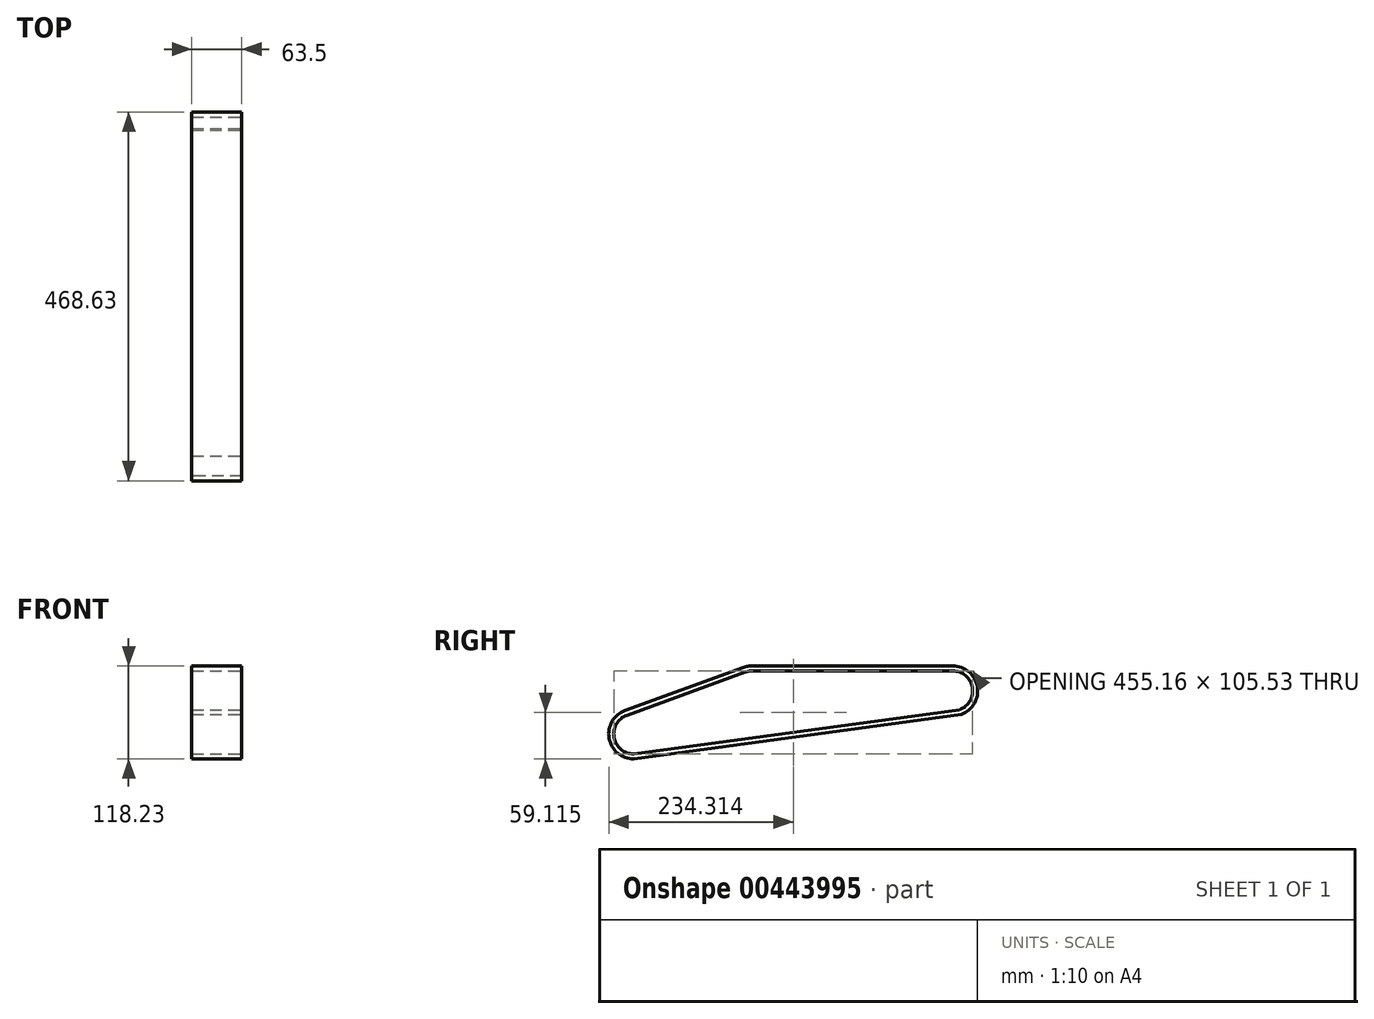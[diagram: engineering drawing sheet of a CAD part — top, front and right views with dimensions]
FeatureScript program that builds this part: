
annotation { "Feature Type Name" : "Feature", "Feature Type Description" : "" }
export const myFeature = defineFeature(function(context is Context, id is Id, definition is map)
    precondition{}
    {
        {
            var Q0;
            Q0=qCreatedBy(makeId("Front.planeOp"),FACE);
            var sketch = newSketch(context, id + "F0", { "sketchPlane" : qUnion([Q0])});
            skLineSegment(sketch, "E0.bottom", {"start": v(0, 0) * mm, "end": v(63.5, 0) * mm});
            skLineSegment(sketch, "E0.top", {"start": v(0, 6.35) * mm, "end": v(63.5, 6.35) * mm});
            skLineSegment(sketch, "E0.left", {"start": v(0, 0) * mm, "end": v(0, 6.35) * mm});
            skLineSegment(sketch, "E0.right", {"start": v(63.5, 0) * mm, "end": v(63.5, 6.35) * mm});
            skSolve(sketch);
        }
        {
            var Q0;
            Q0=makeQuery(id+"F0.imprint","IMPRINT",FACE,{"disambiguationData":[TD([[makeQuery(id+"F0.imprint","IMPRINT",EDGE,{"derivedFrom":sQuery(id+"F0.wireOp",EDGE,"E0.bottom")}),1.0]])]});
            extrude(context, id + "F1", {"entities" : qUnion([Q0]), "depth" : 254.76 * mm});
        }
        {
            var Q0;
            Q0=makeQuery(id+"F1.opExtrude","CAP_FACE",FACE,{"disambiguationData":[OSD([sQuery(id+"F0.wireOp",EDGE,"E0.bottom"),sQuery(id+"F0.wireOp",EDGE,"E0.top"),sQuery(id+"F0.wireOp",EDGE,"E0.left"),sQuery(id+"F0.wireOp",EDGE,"E0.right")])],"isStart":false});
            var sketch = newSketch(context, id + "F2", { "sketchPlane" : qUnion([Q0])});
            skLineSegment(sketch, "E1.bottom", {"start": v(0, 0) * mm, "end": v(63.5, 0) * mm});
            skLineSegment(sketch, "E1.top", {"start": v(0, 6.35) * mm, "end": v(63.5, 6.35) * mm});
            skLineSegment(sketch, "E1.left", {"start": v(0, 0) * mm, "end": v(0, 6.35) * mm});
            skLineSegment(sketch, "E1.right", {"start": v(63.5, 0) * mm, "end": v(63.5, 6.35) * mm});
            skLineSegment(sketch, "E2", {"start": v(0, 0) * mm, "end": v(0, -25.4) * mm});
            skLineSegment(sketch, "E3", {"start": v(0, -25.4) * mm, "end": v(63.5, -25.4) * mm});
            skSolve(sketch);
        }
        {
            var Q0;
            Q0=makeQuery(id+"F2.imprint","IMPRINT",FACE,{"disambiguationData":[TD([[makeQuery(id+"F2.imprint","IMPRINT",EDGE,{"derivedFrom":sQuery(id+"F2.wireOp",EDGE,"E1.bottom")}),1.0]])]});
            var Q1;
            Q1=sQuery(id+"F2.wireOp",EDGE,"E3");
            revolve(context, id + "F3", {"operationType" : NewBodyOperationType.ADD, "entities" : qUnion([Q0]), "axis" : qUnion([Q1]), "revolveType" : RevolveType.ONE_DIRECTION, "angle" : 20 * degree});
        }
        {
            var Q0;
            Q0=makeQuery(id+"F3.opRevolve","CAP_FACE",FACE,{"disambiguationData":[OSD([sQuery(id+"F2.wireOp",EDGE,"E1.bottom"),sQuery(id+"F2.wireOp",EDGE,"E1.top"),sQuery(id+"F2.wireOp",EDGE,"E1.left"),sQuery(id+"F2.wireOp",EDGE,"E1.right")])],"isStart":false});
            var sketch = newSketch(context, id + "F4", { "sketchPlane" : qUnion([Q0])});
            skLineSegment(sketch, "E4.bottom", {"start": v(0, 88.67) * mm, "end": v(63.5, 88.67) * mm});
            skLineSegment(sketch, "E4.top", {"start": v(0, 95.02) * mm, "end": v(63.5, 95.02) * mm});
            skLineSegment(sketch, "E4.left", {"start": v(0, 88.67) * mm, "end": v(0, 95.02) * mm});
            skLineSegment(sketch, "E4.right", {"start": v(63.5, 88.67) * mm, "end": v(63.5, 95.02) * mm});
            skSolve(sketch);
        }
        {
            var Q0;
            Q0=makeQuery(id+"F4.imprint","IMPRINT",FACE,{"disambiguationData":[TD([[makeQuery(id+"F4.imprint","IMPRINT",EDGE,{"derivedFrom":sQuery(id+"F4.wireOp",EDGE,"E4.bottom")}),1.0]])]});
            extrude(context, id + "F5", {"entities" : qUnion([Q0]), "operationType" : NewBodyOperationType.ADD, "depth" : 160.02 * mm});
        }
        {
            var Q0;
            Q0=makeQuery(id+"F5.opExtrude","CAP_FACE",FACE,{"disambiguationData":[OSD([sQuery(id+"F4.wireOp",EDGE,"E4.bottom"),sQuery(id+"F4.wireOp",EDGE,"E4.top"),sQuery(id+"F4.wireOp",EDGE,"E4.left"),sQuery(id+"F4.wireOp",EDGE,"E4.right")])],"isStart":false});
            var sketch = newSketch(context, id + "F6", { "sketchPlane" : qUnion([Q0])});
            skLineSegment(sketch, "E5.bottom", {"start": v(0, 88.67) * mm, "end": v(63.5, 88.67) * mm});
            skLineSegment(sketch, "E5.top", {"start": v(0, 95.02) * mm, "end": v(63.5, 95.02) * mm});
            skLineSegment(sketch, "E5.left", {"start": v(0, 88.67) * mm, "end": v(0, 95.02) * mm});
            skLineSegment(sketch, "E5.right", {"start": v(63.5, 88.67) * mm, "end": v(63.5, 95.02) * mm});
            skLineSegment(sketch, "E6", {"start": v(0, 88.67) * mm, "end": v(0, 63.27) * mm});
            skLineSegment(sketch, "E7", {"start": v(0, 63.27) * mm, "end": v(63.5, 63.27) * mm});
            skSolve(sketch);
        }
        {
            var Q0;
            Q0=makeQuery(id+"F6.imprint","IMPRINT",FACE,{"disambiguationData":[TD([[makeQuery(id+"F6.imprint","IMPRINT",EDGE,{"derivedFrom":sQuery(id+"F6.wireOp",EDGE,"E5.bottom")}),1.0]])]});
            var Q1;
            Q1=sQuery(id+"F6.wireOp",EDGE,"E7");
            revolve(context, id + "F7", {"operationType" : NewBodyOperationType.ADD, "entities" : qUnion([Q0]), "axis" : qUnion([Q1]), "revolveType" : RevolveType.ONE_DIRECTION, "angle" : 160 * degree});
        }
        {
            var Q0;
            Q0=makeQuery(id+"F1.opExtrude","CAP_FACE",FACE,{"disambiguationData":[OSD([sQuery(id+"F0.wireOp",EDGE,"E0.bottom"),sQuery(id+"F0.wireOp",EDGE,"E0.top"),sQuery(id+"F0.wireOp",EDGE,"E0.left"),sQuery(id+"F0.wireOp",EDGE,"E0.right")])],"isStart":true});
            var sketch = newSketch(context, id + "F8", { "sketchPlane" : qUnion([Q0])});
            skLineSegment(sketch, "E8.bottom", {"start": v(0, 0) * mm, "end": v(-63.5, 0) * mm});
            skLineSegment(sketch, "E8.top", {"start": v(0, 6.35) * mm, "end": v(-63.5, 6.35) * mm});
            skLineSegment(sketch, "E8.left", {"start": v(0, 0) * mm, "end": v(0, 6.35) * mm});
            skLineSegment(sketch, "E8.right", {"start": v(-63.5, 0) * mm, "end": v(-63.5, 6.35) * mm});
            skLineSegment(sketch, "E9", {"start": v(-63.5, 0) * mm, "end": v(-63.5, -25.4) * mm});
            skLineSegment(sketch, "E10", {"start": v(-63.5, -25.4) * mm, "end": v(0, -25.4) * mm});
            skSolve(sketch);
        }
        {
            var Q0;
            Q0=makeQuery(id+"F8.imprint","IMPRINT",FACE,{"disambiguationData":[TD([[makeQuery(id+"F8.imprint","IMPRINT",EDGE,{"derivedFrom":sQuery(id+"F8.wireOp",EDGE,"E8.bottom")}),-1.0]])]});
            var Q1;
            Q1=sQuery(id+"F8.wireOp",EDGE,"E10");
            revolve(context, id + "F9", {"operationType" : NewBodyOperationType.ADD, "entities" : qUnion([Q0]), "axis" : qUnion([Q1]), "revolveType" : RevolveType.ONE_DIRECTION, "angle" : 160 * degree});
        }
        {
            var Q0;
            Q0=makeQuery(id+"F9.boolean.opBoolean","MERGE",FACE,{"derivedFrom":[makeQuery(id+"F7.boolean.opBoolean","MERGE",FACE,{"derivedFrom":[makeQuery(id+"F5.boolean.opBoolean","MERGE",FACE,{"derivedFrom":[makeQuery(id+"F3.boolean.opBoolean","MERGE",FACE,{"derivedFrom":[makeQuery(id+"F1.opExtrude","SWEPT_FACE",FACE,{"disambiguationData":[OSD([sQuery(id+"F0.wireOp",EDGE,"E0.right")])]}),makeQuery(id+"F3.opRevolve","SWEPT_FACE",FACE,{"disambiguationData":[OSD([sQuery(id+"F2.wireOp",EDGE,"E1.right")])]})]}),makeQuery(id+"F5.opExtrude","SWEPT_FACE",FACE,{"disambiguationData":[OSD([sQuery(id+"F4.wireOp",EDGE,"E4.right")])]})]}),makeQuery(id+"F7.opRevolve","SWEPT_FACE",FACE,{"disambiguationData":[OSD([sQuery(id+"F6.wireOp",EDGE,"E5.right")])]})]}),makeQuery(id+"F9.opRevolve","SWEPT_FACE",FACE,{"disambiguationData":[OSD([sQuery(id+"F8.wireOp",EDGE,"E8.right")])]})]});
            var sketch = newSketch(context, id + "F10", { "sketchPlane" : qUnion([Q0])});
            skLineSegment(sketch, "E11", {"start": v(-405.13, -111.88) * mm, "end": v(10.86, -55.24) * mm});
            skLineSegment(sketch, "E12", {"start": v(10.86, -55.24) * mm, "end": v(8.69, -49.27) * mm});
            skLineSegment(sketch, "E13", {"start": v(8.69, -49.27) * mm, "end": v(-405.13, -105.53) * mm});
            skLineSegment(sketch, "E14", {"start": v(-405.13, -105.53) * mm, "end": v(-405.13, -111.88) * mm});
            skSolve(sketch);
        }
        {
            var Q0;
            Q0=makeQuery(id+"F10.imprint","IMPRINT",FACE,{"disambiguationData":[TD([[makeQuery(id+"F10.imprint","IMPRINT",EDGE,{"derivedFrom":sQuery(id+"F10.wireOp",EDGE,"E11")}),1.0]])]});
            extrude(context, id + "F11", {"entities" : qUnion([Q0]), "operationType" : NewBodyOperationType.ADD, "oppositeDirection" : true, "depth" : 63.5 * mm});
        }
    });
